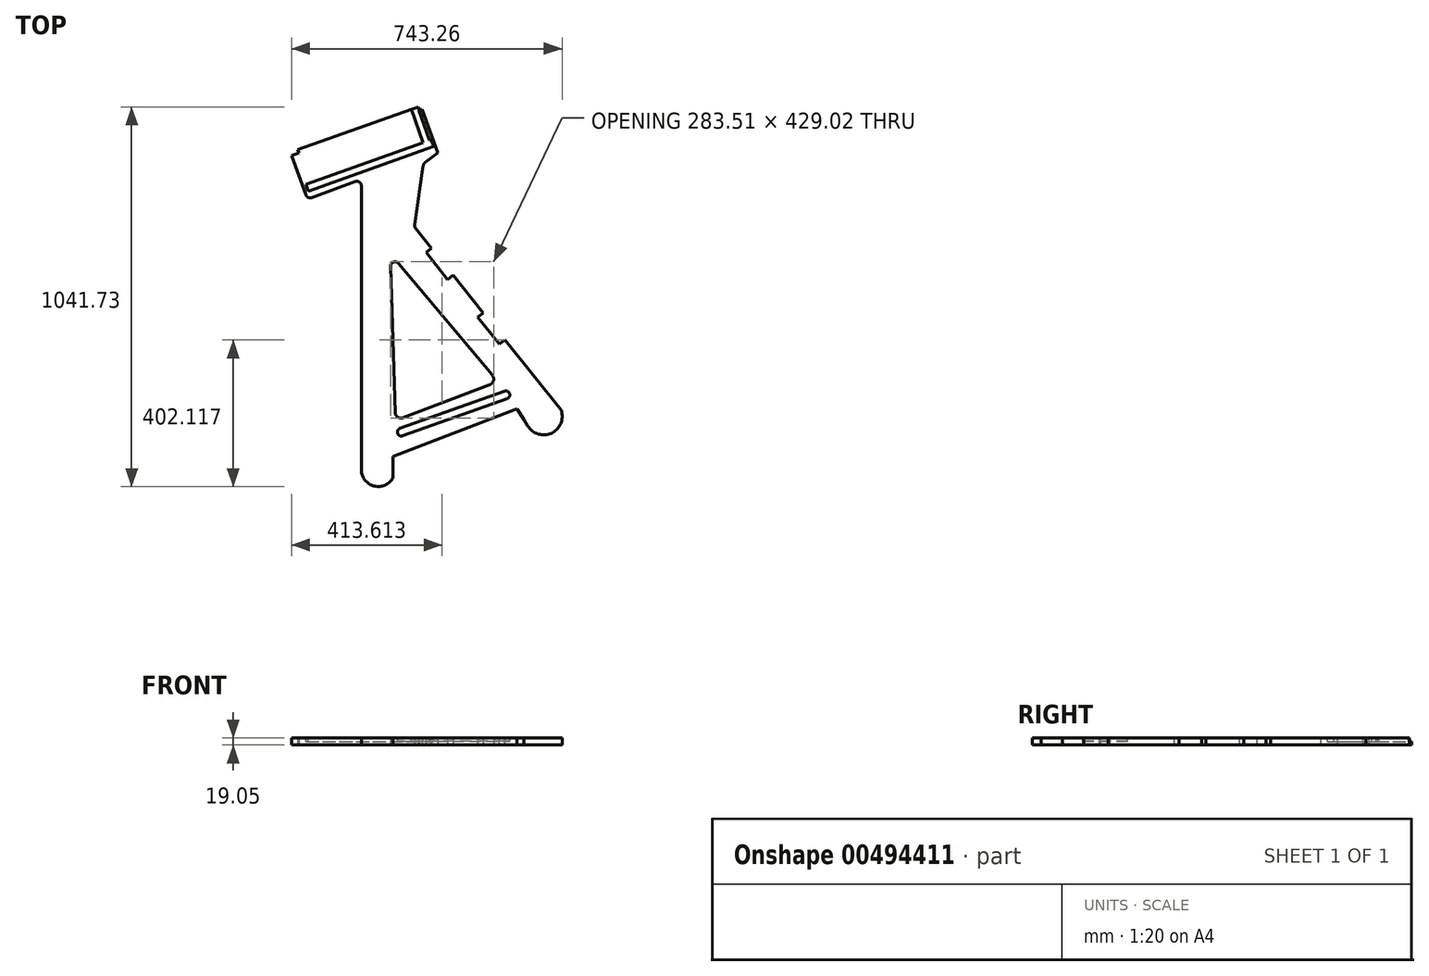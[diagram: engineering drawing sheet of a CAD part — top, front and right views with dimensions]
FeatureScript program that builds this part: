
annotation { "Feature Type Name" : "Feature", "Feature Type Description" : "" }
export const myFeature = defineFeature(function(context is Context, id is Id, definition is map)
    precondition{}
    {
        {
            var Q0;
            Q0=qCreatedBy(makeId("Top.planeOp"),FACE);
            var sketch = newSketch(context, id + "F0", { "sketchPlane" : qUnion([Q0])});
            skLineSegment(sketch, "E0", {"start": v(-306.62, -10.3) * mm, "end": v(-306.88, -10.27) * mm});
            skLineSegment(sketch, "E1", {"start": v(732.44, -265.55) * mm, "end": v(732.44, 429.81) * mm});
            skPoint(sketch, "E2.visualSharp", {"position": v(732.44, -332.19) * mm});
            skPoint(sketch, "E3.visualSharp", {"position": v(834.04, -332.76) * mm});
            skLineSegment(sketch, "E4", {"start": v(902.24, 568.5) * mm, "end": v(878.6, 406.65) * mm});
            skLineSegment(sketch, "E5", {"start": v(732.44, 429.81) * mm, "end": v(732.44, 513.2) * mm});
            skLineSegment(sketch, "E6", {"start": v(715.35, 525.12) * mm, "end": v(596.17, 481.24) * mm});
            skLineSegment(sketch, "E7", {"start": v(579.87, 488.77) * mm, "end": v(540.37, 596.03) * mm});
            skLineSegment(sketch, "E8", {"start": v(540.37, 596.03) * mm, "end": v(561.03, 603.39) * mm});
            skLineSegment(sketch, "E9", {"start": v(899.3, 723.83) * mm, "end": v(941.9, 604.19) * mm});
            skLineSegment(sketch, "E10", {"start": v(906.95, 576.64) * mm, "end": v(941.9, 604.19) * mm});
            skLineSegment(sketch, "E11", {"start": v(540.37, 596.03) * mm, "end": v(561.03, 603.39) * mm, "construction": true});
            skPoint(sketch, "E12.visualSharp", {"position": v(1175.92, -180.14) * mm});
            skLineSegment(sketch, "E13", {"start": v(825.21, -108.15) * mm, "end": v(812.23, 291.9) * mm});
            skLineSegment(sketch, "E14", {"start": v(834.65, 300.48) * mm, "end": v(1091.88, -6.1) * mm});
            skPoint(sketch, "E15.visualSharp", {"position": v(811.04, 328.62) * mm});
            skArc(sketch, "E15.filletArc", {"start": v(834.65, 300.48) * mm, "mid": v(820.38, 304.18) * mm, "end": v(812.23, 291.9) * mm});
            skLineSegment(sketch, "E16", {"start": v(881.25, 396.88) * mm, "end": v(1280.84, -102.55) * mm});
            skLineSegment(sketch, "E17", {"start": v(1185.54, -137.77) * mm, "end": v(1280.84, -102.55) * mm, "construction": true});
            skArc(sketch, "E18", {"start": v(1189.3, -145.4) * mm, "mid": v(1254.36, -165.18) * mm, "end": v(1280.84, -102.55) * mm});
            skLineSegment(sketch, "E19", {"start": v(819.42, -286.78) * mm, "end": v(819.42, -229.12) * mm});
            skLineSegment(sketch, "E20", {"start": v(923.23, 732.35) * mm, "end": v(1268.85, -238.36) * mm, "construction": true});
            skPoint(sketch, "E21.visualSharp", {"position": v(1185.54, -137.77) * mm});
            skPoint(sketch, "E22.visualSharp", {"position": v(877.8, 401.2) * mm});
            skArc(sketch, "E22.filletArc", {"start": v(878.6, 406.65) * mm, "mid": v(878.9, 401.5) * mm, "end": v(881.25, 396.88) * mm});
            skPoint(sketch, "E23.visualSharp", {"position": v(902.97, 573.5) * mm});
            skArc(sketch, "E23.filletArc", {"start": v(906.95, 576.64) * mm, "mid": v(903.81, 573.02) * mm, "end": v(902.24, 568.5) * mm});
            skArc(sketch, "E24.filletArc", {"start": v(732.44, 513.2) * mm, "mid": v(727, 523.62) * mm, "end": v(715.35, 525.12) * mm});
            skLineSegment(sketch, "E25", {"start": v(557.84, 612.36) * mm, "end": v(888.53, 730.1) * mm});
            skLineSegment(sketch, "E26", {"start": v(557.84, 612.36) * mm, "end": v(561.03, 603.39) * mm});
            skLineSegment(sketch, "E27", {"start": v(888.53, 730.1) * mm, "end": v(891.73, 721.13) * mm});
            skLineSegment(sketch, "E28.trimOffspring", {"start": v(891.73, 721.13) * mm, "end": v(899.3, 723.83) * mm, "construction": true});
            skLineSegment(sketch, "E29.trimOffspring", {"start": v(891.73, 721.13) * mm, "end": v(899.3, 723.83) * mm});
            skLineSegment(sketch, "E30", {"start": v(1189.3, -145.4) * mm, "end": v(1178.65, -128.04) * mm});
            skLineSegment(sketch, "E31", {"start": v(540.37, 596.03) * mm, "end": v(914.16, -419.2) * mm, "construction": true});
            skLineSegment(sketch, "E32", {"start": v(819.42, -229.12) * mm, "end": v(1159.46, -98.97) * mm});
            skLineSegment(sketch, "E33", {"start": v(1178.65, -128.04) * mm, "end": v(1159.46, -98.97) * mm});
            skLineSegment(sketch, "E34", {"start": v(847.62, -123.03) * mm, "end": v(1085.13, -32.12) * mm});
            skArc(sketch, "E35", {"start": v(732.44, -265.55) * mm, "mid": v(767.6, -310.31) * mm, "end": v(819.42, -286.78) * mm});
            skLineSegment(sketch, "E36", {"start": v(1247.81, -179.28) * mm, "end": v(691.82, -377.24) * mm, "construction": true});
            skPoint(sketch, "E37.visualSharp", {"position": v(584.25, 476.85) * mm});
            skArc(sketch, "E37.filletArc", {"start": v(579.87, 488.77) * mm, "mid": v(586.46, 481.63) * mm, "end": v(596.17, 481.24) * mm});
            skPoint(sketch, "E38.visualSharp", {"position": v(1106.77, -23.84) * mm});
            skArc(sketch, "E38.filletArc", {"start": v(1085.13, -32.12) * mm, "mid": v(1095.21, -20.85) * mm, "end": v(1091.88, -6.1) * mm});
            skPoint(sketch, "E39.visualSharp", {"position": v(825.97, -131.32) * mm});
            skArc(sketch, "E39.filletArc", {"start": v(825.21, -108.15) * mm, "mid": v(832.58, -121.37) * mm, "end": v(847.62, -123.03) * mm});
            skLineSegment(sketch, "E40", {"start": v(819.42, -286.78) * mm, "end": v(540.37, 596.03) * mm, "construction": true});
            skSolve(sketch);
        }
        {
            var Q0;
            Q0=makeQuery(id+"F0.imprint","IMPRINT",FACE,{"disambiguationData":[TD([[makeQuery(id+"F0.imprint","IMPRINT",EDGE,{"derivedFrom":sQuery(id+"F0.wireOp",EDGE,"oAVC5DI8-kh1G-Qbfy-uwvq-Txyh6lFHP0Ui")}),1.0]])]});
            var Q1;
            Q1=makeQuery(id+"F0.imprint","IMPRINT",FACE,{"disambiguationData":[TD([[makeQuery(id+"F0.imprint","IMPRINT",EDGE,{"derivedFrom":sQuery(id+"F0.wireOp",EDGE,"E1")}),-1.0]])]});
            extrude(context, id + "F1", {"entities" : qUnion([Q0, Q1]), "depth" : 19.05 * mm});
        }
        {
            var Q0;
            Q0=makeQuery(id+"F1.opExtrude","CAP_FACE",FACE,{"disambiguationData":[OSD([sQuery(id+"F0.wireOp",EDGE,"E1"),sQuery(id+"F0.wireOp",EDGE,"G0y4bu0m-BWtu-Z1BD-zRkf-oovVnx2JfWYb"),sQuery(id+"F0.wireOp",EDGE,"JKyS3Y8j-kBsw-wtws-iH0O-fFm78A80juFg"),sQuery(id+"F0.wireOp",EDGE,"7wI2reVj-oknS-nbr6-NEhj-tmmQak3yPgpr"),sQuery(id+"F0.wireOp",EDGE,"OE1zSFFg-K3dP-ErGM-cdOK-dd3cl9o4Xoav"),sQuery(id+"F0.wireOp",EDGE,"GfWBLkyY-Kkl3-p4zT-R0sz-4QZl2egGdYTh"),sQuery(id+"F0.wireOp",EDGE,"E2.filletArc"),sQuery(id+"F0.wireOp",EDGE,"E3.filletArc"),sQuery(id+"F0.wireOp",EDGE,"e34a206c-400c-4626-8d55-ad7425813022.filletArc"),sQuery(id+"F0.wireOp",EDGE,"E4"),sQuery(id+"F0.wireOp",EDGE,"E5"),sQuery(id+"F0.wireOp",EDGE,"E6"),sQuery(id+"F0.wireOp",EDGE,"E7"),sQuery(id+"F0.wireOp",EDGE,"E8"),sQuery(id+"F0.wireOp",EDGE,"E9"),sQuery(id+"F0.wireOp",EDGE,"E10"),sQuery(id+"F0.wireOp",EDGE,"2dwz68pA-47ym-ayAl-zs7R-NUUpSdQx5Jh0"),sQuery(id+"F0.wireOp",EDGE,"E12.filletArc")])],"isStart":false});
            var sketch = newSketch(context, id + "F2", { "sketchPlane" : qUnion([Q0])});
            skLineSegment(sketch, "E41", {"start": v(845.7, -172.6) * mm, "end": v(1132.84, -70.36) * mm});
            skLineSegment(sketch, "E42", {"start": v(1125.6, -50.02) * mm, "end": v(838.45, -152.25) * mm});
            skLineSegment(sketch, "E43.0", {"start": v(540.37, 596.03) * mm, "end": v(777.78, -334.38) * mm, "construction": true});
            skLineSegment(sketch, "E44.0", {"start": v(878.4, -322.07) * mm, "end": v(1232.82, -195.88) * mm, "construction": true});
            skArc(sketch, "E45", {"start": v(838.45, -152.25) * mm, "mid": v(831.9, -166.04) * mm, "end": v(845.7, -172.6) * mm});
            skArc(sketch, "E46", {"start": v(1132.84, -70.36) * mm, "mid": v(1139.38, -56.56) * mm, "end": v(1125.6, -50.02) * mm});
            skSolve(sketch);
        }
        {
            var Q0;
            Q0=qSketchRegion(id+"F2",true);
            extrude(context, id + "F3", {"entities" : qUnion([Q0]), "operationType" : NewBodyOperationType.REMOVE, "oppositeDirection" : true, "depth" : 8.47 * mm});
        }
        {
            var Q0;
            Q0=makeQuery(id+"F1.opExtrude","CAP_FACE",FACE,{"disambiguationData":[OSD([sQuery(id+"F0.wireOp",EDGE,"E1"),sQuery(id+"F0.wireOp",EDGE,"E2.filletArc"),sQuery(id+"F0.wireOp",EDGE,"E3.filletArc"),sQuery(id+"F0.wireOp",EDGE,"E4"),sQuery(id+"F0.wireOp",EDGE,"E5"),sQuery(id+"F0.wireOp",EDGE,"E6"),sQuery(id+"F0.wireOp",EDGE,"E7"),sQuery(id+"F0.wireOp",EDGE,"E8"),sQuery(id+"F0.wireOp",EDGE,"E9"),sQuery(id+"F0.wireOp",EDGE,"E10"),sQuery(id+"F0.wireOp",EDGE,"E13"),sQuery(id+"F0.wireOp",EDGE,"E14"),sQuery(id+"F0.wireOp",EDGE,"E15.filletArc"),sQuery(id+"F0.wireOp",EDGE,"O38EEshE-uP5z-nFdx-e3qj-11sBSmLcHE88"),sQuery(id+"F0.wireOp",EDGE,"b6148c74-efb1-4f58-bf84-b4f1c3a6a91b"),sQuery(id+"F0.wireOp",EDGE,"E16"),sQuery(id+"F0.wireOp",EDGE,"E18"),sQuery(id+"F0.wireOp",EDGE,"E19"),sQuery(id+"F0.wireOp",EDGE,"mhekoGqz-hg7g-Awbu-1WS0-d6fdl79PSdHc"),sQuery(id+"F0.wireOp",EDGE,"5Wj1d7Zn-DfYv-PjeH-97pm-uPEhj1uLzUow"),sQuery(id+"F0.wireOp",EDGE,"440a19d6-b247-49e8-bacf-2963a67fc6c6.filletArc"),sQuery(id+"F0.wireOp",EDGE,"E21.filletArc"),sQuery(id+"F0.wireOp",EDGE,"E22.filletArc"),sQuery(id+"F0.wireOp",EDGE,"E23.filletArc"),sQuery(id+"F0.wireOp",EDGE,"E24.filletArc")])],"isStart":false});
            var sketch = newSketch(context, id + "F4", { "sketchPlane" : qUnion([Q0])});
            skLineSegment(sketch, "E47.bottom", {"start": v(586.26, 498.62) * mm, "end": v(926.44, 619.74) * mm});
            skLineSegment(sketch, "E47.top", {"start": v(579.7, 517.04) * mm, "end": v(902.22, 631.88) * mm});
            skLineSegment(sketch, "E47.left", {"start": v(586.26, 498.62) * mm, "end": v(579.7, 517.04) * mm});
            skLineSegment(sketch, "E48", {"start": v(920, 637.82) * mm, "end": v(891.85, 716.88) * mm});
            skLineSegment(sketch, "E49", {"start": v(874.2, 710.6) * mm, "end": v(902.22, 631.88) * mm});
            skLineSegment(sketch, "E50", {"start": v(874.2, 710.6) * mm, "end": v(869.65, 723.38) * mm});
            skPoint(sketch, "E51.endSnap0", {"position": v(895.51, 722.48) * mm});
            skLineSegment(sketch, "E52", {"start": v(891.85, 716.88) * mm, "end": v(890.5, 720.7) * mm});
            skLineSegment(sketch, "E53", {"start": v(891.73, 721.13) * mm, "end": v(890.5, 720.7) * mm});
            skLineSegment(sketch, "E54", {"start": v(891.73, 721.13) * mm, "end": v(888.53, 730.1) * mm});
            skLineSegment(sketch, "E55", {"start": v(888.53, 730.1) * mm, "end": v(869.65, 723.38) * mm});
            skLineSegment(sketch, "E56", {"start": v(926.44, 619.74) * mm, "end": v(930.6, 621.22) * mm});
            skLineSegment(sketch, "E57", {"start": v(930.6, 621.22) * mm, "end": v(924.16, 639.3) * mm});
            skLineSegment(sketch, "E58", {"start": v(924.16, 639.3) * mm, "end": v(920, 637.82) * mm});
            skPoint(sketch, "E59.orphan", {"position": v(920.95, 638.16) * mm});
            skPoint(sketch, "E60.orphan", {"position": v(919.88, 638.16) * mm});
            skSolve(sketch);
        }
        {
            var Q0;
            Q0=qSketchRegion(id+"F4",true);
            extrude(context, id + "F5", {"entities" : qUnion([Q0]), "operationType" : NewBodyOperationType.REMOVE, "oppositeDirection" : true, "depth" : 9.52 * mm});
        }
        {
            var Q0;
            Q0=makeQuery(id+"F1.opExtrude","SWEPT_FACE",FACE,{"disambiguationData":[OSD([sQuery(id+"F0.wireOp",EDGE,"E16")])]});
            var sketch = newSketch(context, id + "F6", { "sketchPlane" : qUnion([Q0])});
            skPoint(sketch, "E61.0", {"position": v(-240.64, 0) * mm});
            skLineSegment(sketch, "E62.bottom", {"start": v(-310.5, 0) * mm, "end": v(-405.25, 0) * mm});
            skLineSegment(sketch, "E62.top", {"start": v(-310.5, 19.05) * mm, "end": v(-405.25, 19.05) * mm});
            skLineSegment(sketch, "E62.left", {"start": v(-310.5, 0) * mm, "end": v(-310.5, 19.05) * mm});
            skLineSegment(sketch, "E63.1.0.0", {"start": v(-537.61, 0) * mm, "end": v(-632.35, 0) * mm});
            skLineSegment(sketch, "E63.1.0.2", {"start": v(-537.61, 19.05) * mm, "end": v(-632.35, 19.05) * mm});
            skLineSegment(sketch, "E63.1.0.3", {"start": v(-632.35, 0) * mm, "end": v(-632.35, 19.05) * mm});
            skLineSegment(sketch, "E63.direction1", {"start": v(-405.25, 0) * mm, "end": v(-632.35, 0) * mm, "construction": true});
            skLineSegment(sketch, "E64", {"start": v(-405.25, 19.05) * mm, "end": v(-405.25, 0) * mm});
            skLineSegment(sketch, "E65", {"start": v(-537.61, 19.05) * mm, "end": v(-537.61, 0) * mm});
            skSolve(sketch);
        }
        {
            var Q0;
            Q0 = qSketchRegion(id + "F6", true);
            extrude(context, id + "F7", {"entities" : qUnion([Q0]), "operationType" : NewBodyOperationType.REMOVE, "oppositeDirection" : true, "depth" : 19.05 * mm});
        }
    });
